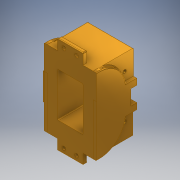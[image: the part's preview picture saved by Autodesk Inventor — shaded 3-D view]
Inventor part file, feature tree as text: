
AUTODESK INVENTOR PART (.ipt)
format: ipt  version: 2017 (Build 210142000, 142)  size: 622,592 bytes
history: native  units: mm
features: extrude x13, sketch x13, projected_geometry x8, plane x3, mirror x3, fillet x2
ambient origin geometry x8: Origin, YZ Plane, XZ Plane, XY Plane, X Axis, Y Axis, Z Axis, Center Point
bodies: Solid1 (feature_tree)
feature tree (42):
  extrude  "Extrusion1"  Depth=54.0mm
  extrude  "Extrusion2"  Depth=54.0mm
  extrude  "Extrusion3"  Depth=5.0mm
  plane  "Work Plane1"
  mirror  "Mirror2"
  mirror  "Mirror3"
  extrude  "Extrusion4"  Depth=4.5mm
  extrude  "Extrusion5"  Depth=6.25mm
  extrude  "Extrusion7"  TaperAngle=90.0deg  [1 undecoded]
  extrude  "Extrusion8"  Depth=25.0mm
  extrude  "Extrusion9"  Depth=30.0mm
  extrude  "Extrusion10"  Depth=7.5mm
  extrude  "Extrusion11"  Depth=12.5mm TaperAngle=0.0deg
  extrude  "Extrusion13"  Depth=4.0mm TaperAngle=0.0deg
  plane  "Work Plane3"
  mirror  "Mirror4"
  extrude  "Extrusion14"  Depth=0.000366mm
  fillet  "Fillet1"  Radius=60.705711mm
  extrude  "Extrusion15"  Depth=1.0mm TaperAngle=0.0deg
  fillet  "Fillet2"  Radius=7.0mm
  sketch  "Sketch2"  dims[d4=90.0mm d5=54.0mm]
  sketch  "Sketch3"  dims[d6=90.0mm d7=54.0mm]
  sketch  "Sketch5"  dims[d8=47.5mm d9=0.0mm d10=5.0mm d11=30.0mm]
  projected_geometry  "Projected Loop1"
  plane  "Work Plane2"
  sketch  "Sketch6"  dims[d12=12.5mm d13=0.0mm d14=4.5mm d15=4.5mm]
  sketch  "Sketch7"  dims[d16=6.25mm d17=6.25mm]
  sketch  "Sketch11"  dims[d18=15.0mm d19=90.0deg]
  sketch  "Sketch12"  dims[d20=90.0deg d21=25.0mm]
  sketch  "Sketch15"  dims[d22=0.0mm d23=30.0mm]
  projected_geometry  "Projected Loop3"
  projected_geometry  "Projected Loop4"
  sketch  "Sketch16"  dims[d24=12.5mm d25=7.5mm]
  projected_geometry  "Projected Loop5"
  sketch  "Sketch17"  dims[d26=12.5mm d27=12.5mm d28=0.0mm]
  projected_geometry  "Projected Loop6"
  projected_geometry  "Projected Loop7"
  sketch  "Sketch18"  dims[d29=45.0mm d35=4.0mm d36=0.0mm]
  sketch  "Sketch19"  dims[d37=47.5mm d38=32.0mm d39=0.000366mm d40=60.705711mm]
  sketch  "Sketch20"  dims[d41=0.001172mm d42=4.0mm d43=0.0mm d45=7.0mm d46=47.5mm d47=7.0mm d48=47.5mm d55=46.0mm d56=58.0mm d59=18.0mm d62=58.0mm d66=16.0mm d67=18.0mm d68=16.0mm d69=16.0mm d70=18.0mm d71=7.0mm d72=0.0mm d73=26.0mm d74=26.0mm d75=30.0mm d76=16.0mm d77=19.0mm d78=52.0mm d79=90.0deg d80=36.0mm d81=58.0mm d82=0.0mm d83=0.0mm d84=0.0mm d85=2.5mm d86=12.0mm d87=3.5mm d88=2.5mm d89=3.2mm d90=4.0mm d97=2.5mm d98=4.1mm d99=3.5mm d100=2.3mm d101=3.5mm d102=11.0mm d103=2.5mm d106=2.5mm d107=3.5mm d108=2.5mm d109=3.2mm d110=2.5mm d111=2.5mm d112=3.5mm d113=6.9mm d114=2.5mm d115=5.5mm d117=54.0mm d118=8.0mm d119=0.0mm d120=8.0mm d121=8.0mm d122=16.0mm d123=6.0mm d124=19.0mm d125=8.0mm d126=8.0mm d127=16.0mm d130=6.0mm d131=19.0mm d132=23.0mm d133=23.0mm d134=58.0mm d135=0.0mm d136=8.0mm d137=0.0mm d138=90.0deg d139=1.396263mm d140=90.0deg d141=15.787291mm d142=1.396263mm d143=14.717306mm d144=75.352856mm d145=3.000844mm d146=0.0mm d147=6.610722mm d148=0.0mm d149=3.664235mm d150=82.513404mm d151=72.352856mm d152=4.0mm d153=0.0mm d154=31.546191mm d155=34.84835mm d156=34.847179mm d157=31.546mm d158=31.415523mm d159=0.001172mm d160=32.0mm d161=0.002969mm d162=19.479459mm d163=0.0mm d164=0.0mm d167=4.0mm d168=0.0mm d169=27.0mm d170=1.0mm d171=0.0mm d172=1.0mm d173=4.0mm d174=33.8mm d175=19.0mm d176=4.0mm d177=18.5mm d180=33.8mm d181=20.0mm d182=0.0mm d183=1.0mm]
  projected_geometry  "Projected Loop8"
  projected_geometry  "Projected Loop9"
note: 1 required parameter value undecoded (feature->parameter linkage not recoverable at this tier; creation-order binding heuristic only, values carry confidence <= 0.55)
